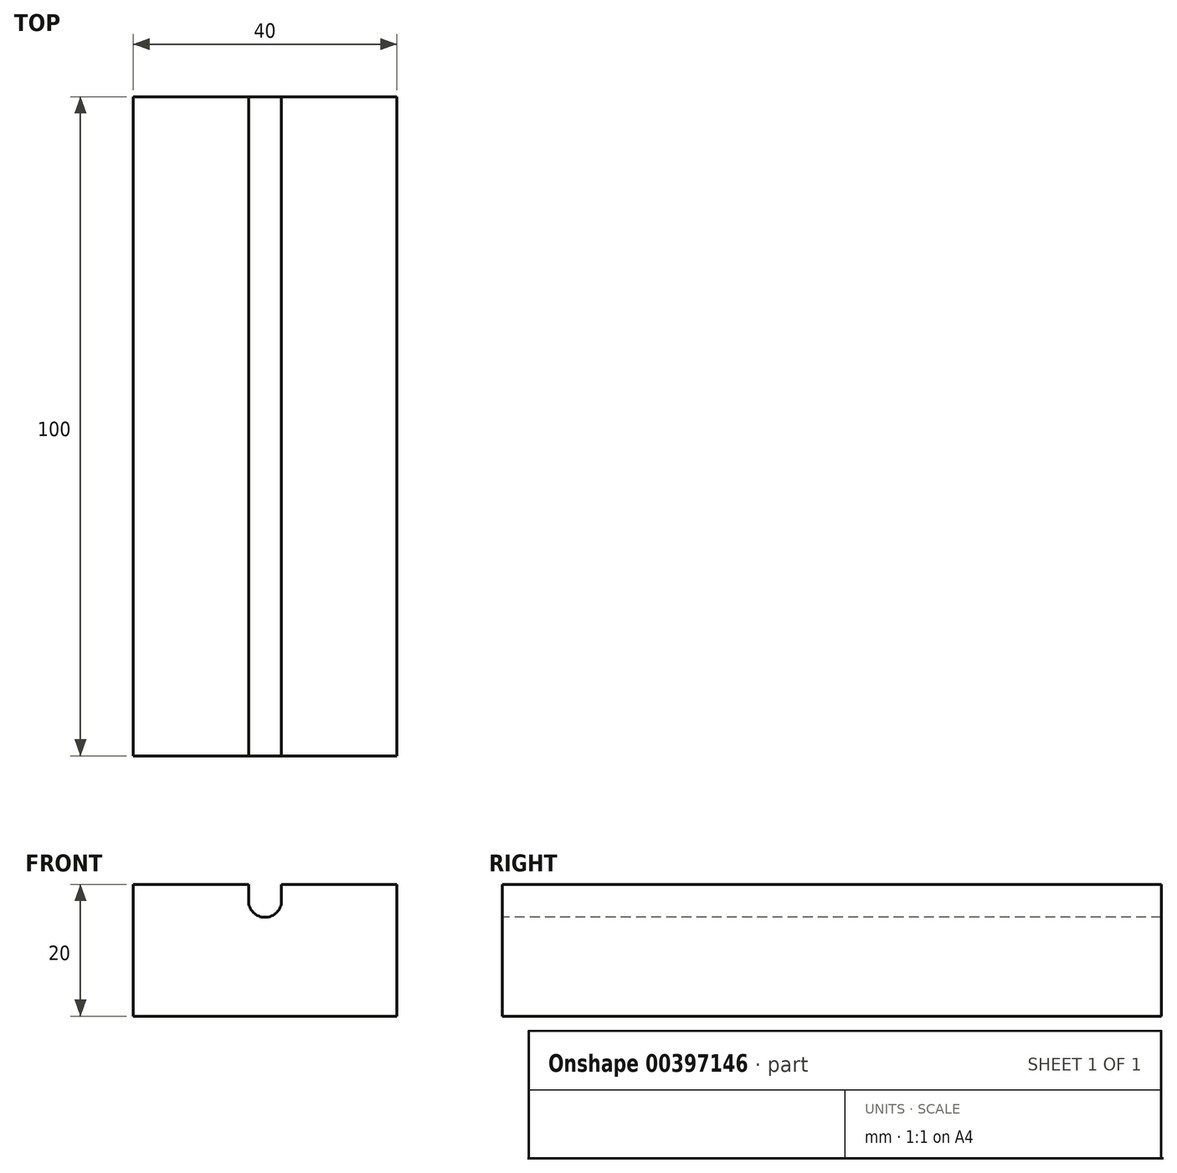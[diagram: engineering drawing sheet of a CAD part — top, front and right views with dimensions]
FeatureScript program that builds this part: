
annotation { "Feature Type Name" : "Feature", "Feature Type Description" : "" }
export const myFeature = defineFeature(function(context is Context, id is Id, definition is map)
    precondition{}
    {
        {
            var Q0;
            Q0=qCreatedBy(makeId("Top.planeOp"),FACE);
            var sketch = newSketch(context, id + "F0", { "sketchPlane" : qUnion([Q0])});
            skLineSegment(sketch, "E0.bottom", {"start": v(-20, 90.37) * mm, "end": v(20, 90.37) * mm});
            skLineSegment(sketch, "E0.top", {"start": v(-20, -9.63) * mm, "end": v(20, -9.63) * mm});
            skLineSegment(sketch, "E0.left", {"start": v(-20, 90.37) * mm, "end": v(-20, -9.63) * mm});
            skLineSegment(sketch, "E0.right", {"start": v(20, 90.37) * mm, "end": v(20, -9.63) * mm});
            skSolve(sketch);
        }
        {
            var Q0;
            Q0=makeQuery(id+"F0.imprint","IMPRINT",FACE,{"disambiguationData":[TD([[makeQuery(id+"F0.imprint","IMPRINT",EDGE,{"derivedFrom":sQuery(id+"F0.wireOp",EDGE,"E0.bottom")}),-1.0]])]});
            extrude(context, id + "F1", {"entities" : qUnion([Q0]), "oppositeDirection" : true, "depth" : 20 * mm});
        }
        {
            var Q0;
            Q0=makeQuery(id+"F1.opExtrude","SWEPT_FACE",FACE,{"disambiguationData":[OSD([sQuery(id+"F0.wireOp",EDGE,"E0.top")])]});
            var sketch = newSketch(context, id + "F2", { "sketchPlane" : qUnion([Q0])});
            skPoint(sketch, "E1", {"position": v(0, -2.5) * mm});
            skCircle(sketch, "E2", {"center": v(0, -2.5) * mm, "radius": 2.5 * mm});
            skLineSegment(sketch, "E3", {"start": v(-2.5, -2.5) * mm, "end": v(-2.5, 0) * mm});
            skLineSegment(sketch, "E4", {"start": v(2.5, -2.5) * mm, "end": v(2.5, 0) * mm});
            skSolve(sketch);
        }
        {
            var Q0;
            Q0 = qSketchRegion(id + "F2", true);
            var Q1;
            {var subQ0=sQuery(id+"F2.wireOp",EDGE,"E4");Q1=makeQuery(id+"F2.imprint","IMPRINT",FACE,{"disambiguationData":[TD([[makeQuery(id+"F2.imprint","IMPRINT",EDGE,{"derivedFrom":subQ0}),1.0]])]});}
            var Q2;
            {var subQ0=sQuery(id+"F2.wireOp",EDGE,"E3");Q2=makeQuery(id+"F2.imprint","IMPRINT",FACE,{"disambiguationData":[TD([[makeQuery(id+"F2.imprint","IMPRINT",EDGE,{"derivedFrom":subQ0}),-1.0]])]});}
            extrude(context, id + "F3", {"entities" : qUnion([Q0, Q1, Q2]), "operationType" : NewBodyOperationType.REMOVE, "endBound" : BoundingType.UP_TO_NEXT, "oppositeDirection" : true, "depth" : 25 * mm});
        }
    });
